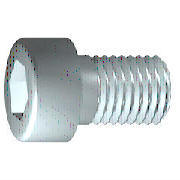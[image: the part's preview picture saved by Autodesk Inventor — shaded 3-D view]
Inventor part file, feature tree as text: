
AUTODESK INVENTOR PART (.ipt)
format: ipt  version: 2021 (Build 250183000, 183)  size: 195,072 bytes
history: native  units: mm (DEFAULTED — no unit token found)
features: sketch x2, extrude x1, plane x1, fillet x1
ambient origin geometry x7: Origin, YZ Plane, XY Plane, X Axis, Y Axis, Z Axis, Center Point
bodies: Solid1 (feature_tree), Body (feature_tree)
feature tree (5):
  extrude  "Slot"  Depth=2.5mm
  plane  "Work Plane1"
  fillet  "Fillet2"  Radius=2.5mm
  sketch  "Sketch1"  dims[d1=4.875mm d2=0.276153mm d3=2.5mm]
  sketch  "Sketch2"  dims[d4=1.1mm d5=60.0deg d6=2.5mm d7=2.5mm d8=2.309401mm d9=4.5mm d10=90.0deg d11=10.0mm d12=0.0mm d13=4.875mm d14=0.0mm d15=0.276052mm d16=0.276053mm d17=0.25mm d19=0.0mm d26=6.0mm d27=45.0deg d28=0.0mm d29=0.0mm d30=0.1mm]
